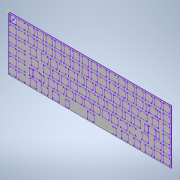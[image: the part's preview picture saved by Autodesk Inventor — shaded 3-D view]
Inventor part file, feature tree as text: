
AUTODESK INVENTOR PART (.ipt)
format: ipt  version: 2020 (Build 240168000, 168)  size: 518,144 bytes
history: native  units: mm
features: other x2, sketch x1, sheet_metal_op x1
ambient origin geometry x8: Origin, YZ Plane, XZ Plane, XY Plane, X Axis, Y Axis, Z Axis, Center Point
bodies: Body1 (feature_tree)
feature tree (4):
  sketch  "Sketch1"  dims[d15=0.5mm d16=0.5mm d17=0.0mm d9=0.5mm d10=0.872665mm d11=0.5mm d12=0.872665mm]
  sheet_metal_op  "Face2"
  other  "Plate2"
  other  "Cut1"
